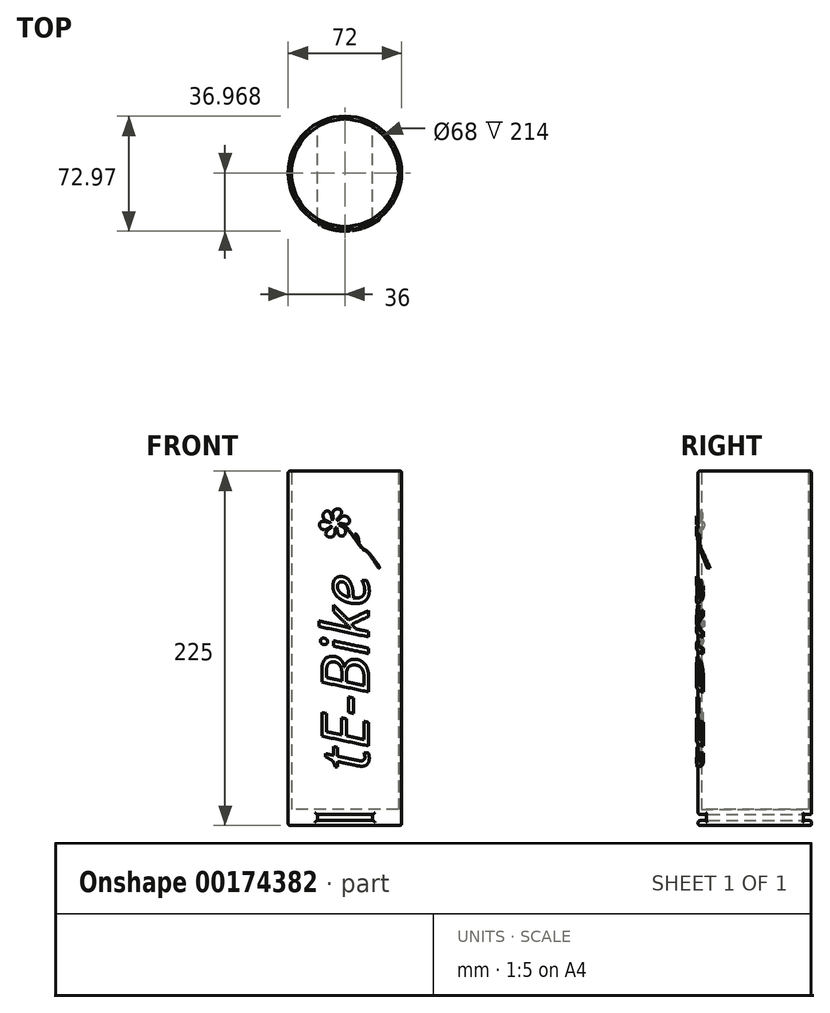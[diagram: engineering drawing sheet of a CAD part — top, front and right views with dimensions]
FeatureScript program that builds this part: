
annotation { "Feature Type Name" : "Feature", "Feature Type Description" : "" }
export const myFeature = defineFeature(function(context is Context, id is Id, definition is map)
    precondition{}
    {
        {
            var Q0;
            Q0=qCreatedBy(makeId("Top.planeOp"),FACE);
            var sketch = newSketch(context, id + "F0", { "sketchPlane" : qUnion([Q0])});
            skCircle(sketch, "E0.0", {"center": v(0, -2.8) * mm, "radius": 36 * mm});
            skLineSegment(sketch, "E1", {"start": v(0, 33.2) * mm, "end": v(0, -38.8) * mm});
            skLineSegment(sketch, "E2", {"start": v(0, -2.8) * mm, "end": v(-36, -2.8) * mm});
            skLineSegment(sketch, "E3", {"start": v(0, -2.8) * mm, "end": v(36, -2.8) * mm});
            skSolve(sketch);
        }
        {
            var Q0;
            Q0=qSketchRegion(id+"F0",true);
            var Q1;
            Q1=makeQuery(id+"F0.imprint","IMPRINT",FACE,{"disambiguationData":[TD([[makeQuery(id+"F0.imprint","IMPRINT",EDGE,{"derivedFrom":sQuery(id+"F0.wireOp",EDGE,"E0.0")}),1.0]])]});
            extrude(context, id + "F1", {"entities" : qUnion([Q0, Q1]), "depth" : 10 * mm});
        }
        {
            var Q0;
            Q0=makeQuery(id+"F1.opExtrude","CAP_FACE",FACE,{"disambiguationData":[OSD([sQuery(id+"F0.wireOp",EDGE,"E0.0")])],"isStart":false});
            var sketch = newSketch(context, id + "F2", { "sketchPlane" : qUnion([Q0])});
            skCircle(sketch, "E4.0", {"center": v(0, -2.8) * mm, "radius": 34 * mm});
            skSolve(sketch);
        }
        {
            var Q0;
            Q0=makeQuery(id+"F2.imprint","IMPRINT",FACE,{"disambiguationData":[TD([[makeQuery(id+"F2.imprint","IMPRINT",EDGE,{"derivedFrom":sQuery(id+"F2.wireOp",EDGE,"E4.0")}),-1.0]])]});
            extrude(context, id + "F3", {"entities" : qUnion([Q0]), "operationType" : NewBodyOperationType.ADD, "depth" : 215 * mm});
        }
        {
            var Q0;
            Q0=qCreatedBy(makeId("Front.planeOp"),FACE);
            var sketch = newSketch(context, id + "F4", { "sketchPlane" : qUnion([Q0])});
            skLineSegment(sketch, "E5", {"start": v(-42.08, 0) * mm, "end": v(47.5, 0) * mm});
            skLineSegment(sketch, "E6.0", {"start": v(-17.5, 3) * mm, "end": v(17.5, 3) * mm});
            skLineSegment(sketch, "E7.0", {"start": v(-17.5, 7) * mm, "end": v(17.5, 7) * mm});
            skLineSegment(sketch, "E8.0", {"start": v(17.5, 3) * mm, "end": v(17.5, 7) * mm});
            skLineSegment(sketch, "E9.0", {"start": v(-17.5, 3) * mm, "end": v(-17.5, 7) * mm});
            skSolve(sketch);
        }
        {
            var Q0;
            Q0=qSketchRegion(id+"F4",true);
            extrude(context, id + "F5", {"entities" : qUnion([Q0]), "operationType" : NewBodyOperationType.REMOVE, "endBound" : BoundingType.THROUGH_ALL, "depth" : 44.2 * mm, "hasSecondDirection" : true, "secondDirectionOppositeDirection" : true, "secondDirectionDepth" : 36.8 * mm});
        }
        {
            var Q0;
            Q0=makeQuery(id+"F3.opExtrude","CAP_EDGE",EDGE,{"disambiguationData":[OSD([sQuery(id+"F2.wireOp",EDGE,"E4.0")])],"isStart":false});
            var Q1;
            Q1=makeQuery(id+"F3.opExtrude","CAP_EDGE",EDGE,{"disambiguationData":[OSD([sQuery(id+"F0.wireOp",EDGE,"E0.0")])],"isStart":false});
            var Q2;
            Q2=makeQuery(id+"F1.opExtrude","CAP_EDGE",EDGE,{"disambiguationData":[OSD([sQuery(id+"F0.wireOp",EDGE,"E0.0")])],"isStart":true});
            var Q3;
            {var subQ0=sQuery(id+"F0.wireOp",EDGE,"E0.0");Q3=makeQuery(id+"F5.boolean.opBoolean","INTERSECT",EDGE,{"disambiguationData":[OD(0.0)],"derivedFrom":[makeQuery(id+"F3.boolean.opBoolean","MERGE",FACE,{"derivedFrom":[makeQuery(id+"F1.opExtrude","SWEPT_FACE",FACE,{"disambiguationData":[OSD([subQ0])]}),makeQuery(id+"F3.opExtrude","SWEPT_FACE",FACE,{"disambiguationData":[OSD([subQ0])]})]}),makeQuery(id+"F5.opExtrude","SWEPT_FACE",FACE,{"disambiguationData":[OSD([sQuery(id+"F4.wireOp",EDGE,"E7.0")])]})]});}
            var Q4;
            {var subQ0=sQuery(id+"F0.wireOp",EDGE,"E0.0");Q4=makeQuery(id+"F5.boolean.opBoolean","INTERSECT",EDGE,{"disambiguationData":[OD(0.0)],"derivedFrom":[makeQuery(id+"F3.boolean.opBoolean","MERGE",FACE,{"derivedFrom":[makeQuery(id+"F1.opExtrude","SWEPT_FACE",FACE,{"disambiguationData":[OSD([subQ0])]}),makeQuery(id+"F3.opExtrude","SWEPT_FACE",FACE,{"disambiguationData":[OSD([subQ0])]})]}),makeQuery(id+"F5.opExtrude","SWEPT_FACE",FACE,{"disambiguationData":[OSD([sQuery(id+"F4.wireOp",EDGE,"E9.0")])]})]});}
            var Q5;
            {var subQ0=sQuery(id+"F0.wireOp",EDGE,"E0.0");Q5=makeQuery(id+"F5.boolean.opBoolean","INTERSECT",EDGE,{"disambiguationData":[OD(0.0)],"derivedFrom":[makeQuery(id+"F3.boolean.opBoolean","MERGE",FACE,{"derivedFrom":[makeQuery(id+"F1.opExtrude","SWEPT_FACE",FACE,{"disambiguationData":[OSD([subQ0])]}),makeQuery(id+"F3.opExtrude","SWEPT_FACE",FACE,{"disambiguationData":[OSD([subQ0])]})]}),makeQuery(id+"F5.opExtrude","SWEPT_FACE",FACE,{"disambiguationData":[OSD([sQuery(id+"F4.wireOp",EDGE,"E6.0")])]})]});}
            var Q6;
            {var subQ0=sQuery(id+"F0.wireOp",EDGE,"E0.0");Q6=makeQuery(id+"F5.boolean.opBoolean","INTERSECT",EDGE,{"disambiguationData":[OD(0.0)],"derivedFrom":[makeQuery(id+"F3.boolean.opBoolean","MERGE",FACE,{"derivedFrom":[makeQuery(id+"F1.opExtrude","SWEPT_FACE",FACE,{"disambiguationData":[OSD([subQ0])]}),makeQuery(id+"F3.opExtrude","SWEPT_FACE",FACE,{"disambiguationData":[OSD([subQ0])]})]}),makeQuery(id+"F5.opExtrude","SWEPT_FACE",FACE,{"disambiguationData":[OSD([sQuery(id+"F4.wireOp",EDGE,"E8.0")])]})]});}
            var Q7;
            {var subQ0=sQuery(id+"F0.wireOp",EDGE,"E0.0");Q7=makeQuery(id+"F5.boolean.opBoolean","INTERSECT",EDGE,{"disambiguationData":[OD(1.0)],"derivedFrom":[makeQuery(id+"F3.boolean.opBoolean","MERGE",FACE,{"derivedFrom":[makeQuery(id+"F1.opExtrude","SWEPT_FACE",FACE,{"disambiguationData":[OSD([subQ0])]}),makeQuery(id+"F3.opExtrude","SWEPT_FACE",FACE,{"disambiguationData":[OSD([subQ0])]})]}),makeQuery(id+"F5.opExtrude","SWEPT_FACE",FACE,{"disambiguationData":[OSD([sQuery(id+"F4.wireOp",EDGE,"E7.0")])]})]});}
            var Q8;
            {var subQ0=sQuery(id+"F0.wireOp",EDGE,"E0.0");Q8=makeQuery(id+"F5.boolean.opBoolean","INTERSECT",EDGE,{"disambiguationData":[OD(1.0)],"derivedFrom":[makeQuery(id+"F3.boolean.opBoolean","MERGE",FACE,{"derivedFrom":[makeQuery(id+"F1.opExtrude","SWEPT_FACE",FACE,{"disambiguationData":[OSD([subQ0])]}),makeQuery(id+"F3.opExtrude","SWEPT_FACE",FACE,{"disambiguationData":[OSD([subQ0])]})]}),makeQuery(id+"F5.opExtrude","SWEPT_FACE",FACE,{"disambiguationData":[OSD([sQuery(id+"F4.wireOp",EDGE,"E9.0")])]})]});}
            var Q9;
            {var subQ0=sQuery(id+"F0.wireOp",EDGE,"E0.0");Q9=makeQuery(id+"F5.boolean.opBoolean","INTERSECT",EDGE,{"disambiguationData":[OD(1.0)],"derivedFrom":[makeQuery(id+"F3.boolean.opBoolean","MERGE",FACE,{"derivedFrom":[makeQuery(id+"F1.opExtrude","SWEPT_FACE",FACE,{"disambiguationData":[OSD([subQ0])]}),makeQuery(id+"F3.opExtrude","SWEPT_FACE",FACE,{"disambiguationData":[OSD([subQ0])]})]}),makeQuery(id+"F5.opExtrude","SWEPT_FACE",FACE,{"disambiguationData":[OSD([sQuery(id+"F4.wireOp",EDGE,"E6.0")])]})]});}
            var Q10;
            {var subQ0=sQuery(id+"F0.wireOp",EDGE,"E0.0");Q10=makeQuery(id+"F5.boolean.opBoolean","INTERSECT",EDGE,{"disambiguationData":[OD(1.0)],"derivedFrom":[makeQuery(id+"F3.boolean.opBoolean","MERGE",FACE,{"derivedFrom":[makeQuery(id+"F1.opExtrude","SWEPT_FACE",FACE,{"disambiguationData":[OSD([subQ0])]}),makeQuery(id+"F3.opExtrude","SWEPT_FACE",FACE,{"disambiguationData":[OSD([subQ0])]})]}),makeQuery(id+"F5.opExtrude","SWEPT_FACE",FACE,{"disambiguationData":[OSD([sQuery(id+"F4.wireOp",EDGE,"E8.0")])]})]});}
            fillet(context, id + "F6", {"entities" : qUnion([Q0, Q1, Q2, Q3, Q4, Q5, Q6, Q7, Q8, Q9, Q10]), "radius" : 1 * mm, "tangentPropagation" : true, "allowEdgeOverflow" : false});
        }
        {
            var Q0;
            Q0=qCreatedBy(makeId("Front.planeOp"),FACE);
            cPlane(context, id + "F7", {"entities" : qUnion([Q0]), "cplaneType" : CPlaneType.OFFSET, "offset" : 40 * mm, "width" : 150 * mm, "height" : 150 * mm});
        }
        {
            var Q0;
            Q0=makeQuery(id+"F1.opExtrude","CAP_FACE",FACE,{"disambiguationData":[OSD([sQuery(id+"F0.wireOp",EDGE,"E0.0")])],"isStart":true});
            var sketch = newSketch(context, id + "F8", { "sketchPlane" : qUnion([Q0])});
            skCircle(sketch, "E10.0", {"center": v(0, 2.8) * mm, "radius": 37 * mm});
            skCircle(sketch, "E11", {"center": v(0, 2.8) * mm, "radius": 36 * mm});
            skCircle(sketch, "E12.0", {"center": v(0, 2.8) * mm, "radius": 52 * mm});
            skSolve(sketch);
        }
        {
            var Q0;
            Q0=makeQuery(id+"F8.imprint","IMPRINT",FACE,{"disambiguationData":[TD([[makeQuery(id+"F8.imprint","IMPRINT",EDGE,{"derivedFrom":sQuery(id+"F8.wireOp",EDGE,"E10.0")}),-1.0]])]});
            extrude(context, id + "F9", {"entities" : qUnion([Q0]), "operationType" : NewBodyOperationType.REMOVE, "oppositeDirection" : true, "depth" : 193 * mm});
        }
        {
            var Q0;
            Q0=qCreatedBy(id+"F7.planeOp",FACE);
            var sketch = newSketch(context, id + "F10", { "sketchPlane" : qUnion([Q0])});
            skText(sketch, "E13", { "text": "tE-Bike", "fontName": "OpenSans-Italic.ttf"});
            skArc(sketch, "E14", {"start": v(-3.71, 191.56) * mm, "mid": v(-9.32, 191.97) * mm, "end": v(-3.74, 191.29) * mm});
            skFitSpline(sketch, "E15", {"points": [v(-4.44, 192.07) * mm, v(-3.7, 191.96) * mm, v(1.7, 191.38) * mm, v(2.88, 194.11) * mm, v(-0.29, 196.47) * mm, v(-4.6, 193.58) * mm], "startDerivative": vector(5.3, -0.47) * mm, "endDerivative": vector(-11.1, -10.08) * mm});
            skFitSpline(sketch, "E16", {"points": [v(-7.81, 193.37) * mm, v(-8.03, 194.06) * mm, v(-9.98, 199.12) * mm, v(-12.95, 198.92) * mm, v(-13.6, 195.04) * mm, v(-9.21, 192.5) * mm], "startDerivative": vector(-2, 4.94) * mm, "endDerivative": vector(14.02, -5.32) * mm});
            skFitSpline(sketch, "E17", {"points": [v(-5.73, 193.56) * mm, v(-5.27, 194.12) * mm, v(-2.09, 198.51) * mm, v(-3.87, 200.9) * mm, v(-7.49, 199.33) * mm, v(-7.22, 194.26) * mm], "startDerivative": vector(3.06, 4.36) * mm, "endDerivative": vector(3.18, -14.65) * mm});
            skFitSpline(sketch, "E18", {"points": [v(-7.56, 191.64) * mm, v(-9.32, 192.1) * mm, v(-14.52, 193.06) * mm, v(-16.29, 190.65) * mm, v(-13.18, 187.75) * mm, v(-8.6, 189.96) * mm], "startDerivative": vector(-5.06, 1.52) * mm, "endDerivative": vector(12.27, 8.61) * mm});
            skFitSpline(sketch, "E19", {"points": [v(-7.65, 190.11) * mm, v(-8.2, 189.64) * mm, v(-12.1, 185.87) * mm, v(-10.76, 183.21) * mm, v(-6.92, 184.12) * mm, v(-6.3, 189.16) * mm], "startDerivative": vector(-3.77, -3.76) * mm, "endDerivative": vector(-0.58, 14.98) * mm});
            skFitSpline(sketch, "E20", {"points": [v(-5.56, 190.04) * mm, v(-5.36, 189.33) * mm, v(-3.55, 184.23) * mm, v(-0.58, 184.34) * mm, v(0.19, 188.2) * mm, v(-4.14, 190.87) * mm], "startDerivative": vector(1.86, -5) * mm, "endDerivative": vector(-13.87, 5.7) * mm});
            skFitSpline(sketch, "E21", {"points": [v(-4.05, 191.41) * mm, v(-3.33, 191.12) * mm, v(-0.67, 189.8) * mm, v(4.27, 184.67) * mm, v(11.89, 175) * mm, v(13.68, 174.1) * mm, v(21.4, 163.4) * mm], "startDerivative": vector(9.65, -3.74) * mm, "endDerivative": vector(34.67, -54.82) * mm});
            skFitSpline(sketch, "E22", {"points": [v(-4.02, 191.8) * mm, v(-3.55, 191.47) * mm, v(-2.82, 191.22) * mm, v(-1.46, 190.56) * mm, v(1.25, 188.85) * mm, v(3.15, 186.69) * mm, v(7.04, 181.69) * mm, v(11.63, 175.78) * mm, v(13.95, 174.35) * mm, v(21.98, 163.45) * mm, v(21.4, 163.4) * mm], "startDerivative": vector(9.05, -8.27) * mm, "endDerivative": vector(-19.5, -1.13) * mm});
            skLineSegment(sketch, "E23", {"start": v(2.3, 177.71) * mm, "end": v(2.65, 177.69) * mm});
            skFitSpline(sketch, "E24", {"points": [v(6.6, 181.9) * mm, v(6.66, 182.2) * mm, v(6.7, 185.11) * mm, v(8.24, 183.2) * mm, v(8.82, 178.87) * mm], "startDerivative": vector(0.72, 1.63) * mm, "endDerivative": vector(-0.07, -12.13) * mm});
            skArc(sketch, "E25", {"start": v(-3.74, 191.29) * mm, "mid": v(-3.72, 191.42) * mm, "end": v(-3.71, 191.56) * mm});
            skLineSegment(sketch, "E26", {"start": v(13.95, 174.35) * mm, "end": v(13.68, 174.1) * mm});
            const initialGuessF10  = {"E13": [0.01506, 0.03516, 0, 1, 0.03]};
            skSetInitialGuess(sketch, initialGuessF10);
            skSolve(sketch);
        }
        {
            var Q0;
            Q0 = qSketchRegion(id + "F10", true);
            extrude(context, id + "F11", {"entities" : qUnion([Q0]), "endBound" : BoundingType.UP_TO_NEXT, "oppositeDirection" : true, "depth" : 25 * mm});
        }
        {
            var Q0;
            Q0=makeQuery(id+"F1.opExtrude","CAP_FACE",FACE,{"disambiguationData":[OSD([sQuery(id+"F0.wireOp",EDGE,"E0.0")])],"isStart":true});
            var sketch = newSketch(context, id + "F12", { "sketchPlane" : qUnion([Q0])});
            skCircle(sketch, "E27", {"center": v(0, 2.8) * mm, "radius": 36.97 * mm});
            skCircle(sketch, "E28.0", {"center": v(0, 2.8) * mm, "radius": 45.77 * mm});
            skSolve(sketch);
        }
        {
            var Q0;
            Q0 = qSketchRegion(id + "F12", true);
            extrude(context, id + "F13", {"entities" : qUnion([Q0]), "operationType" : NewBodyOperationType.REMOVE, "oppositeDirection" : true, "depth" : 253.1 * mm});
        }
    });
